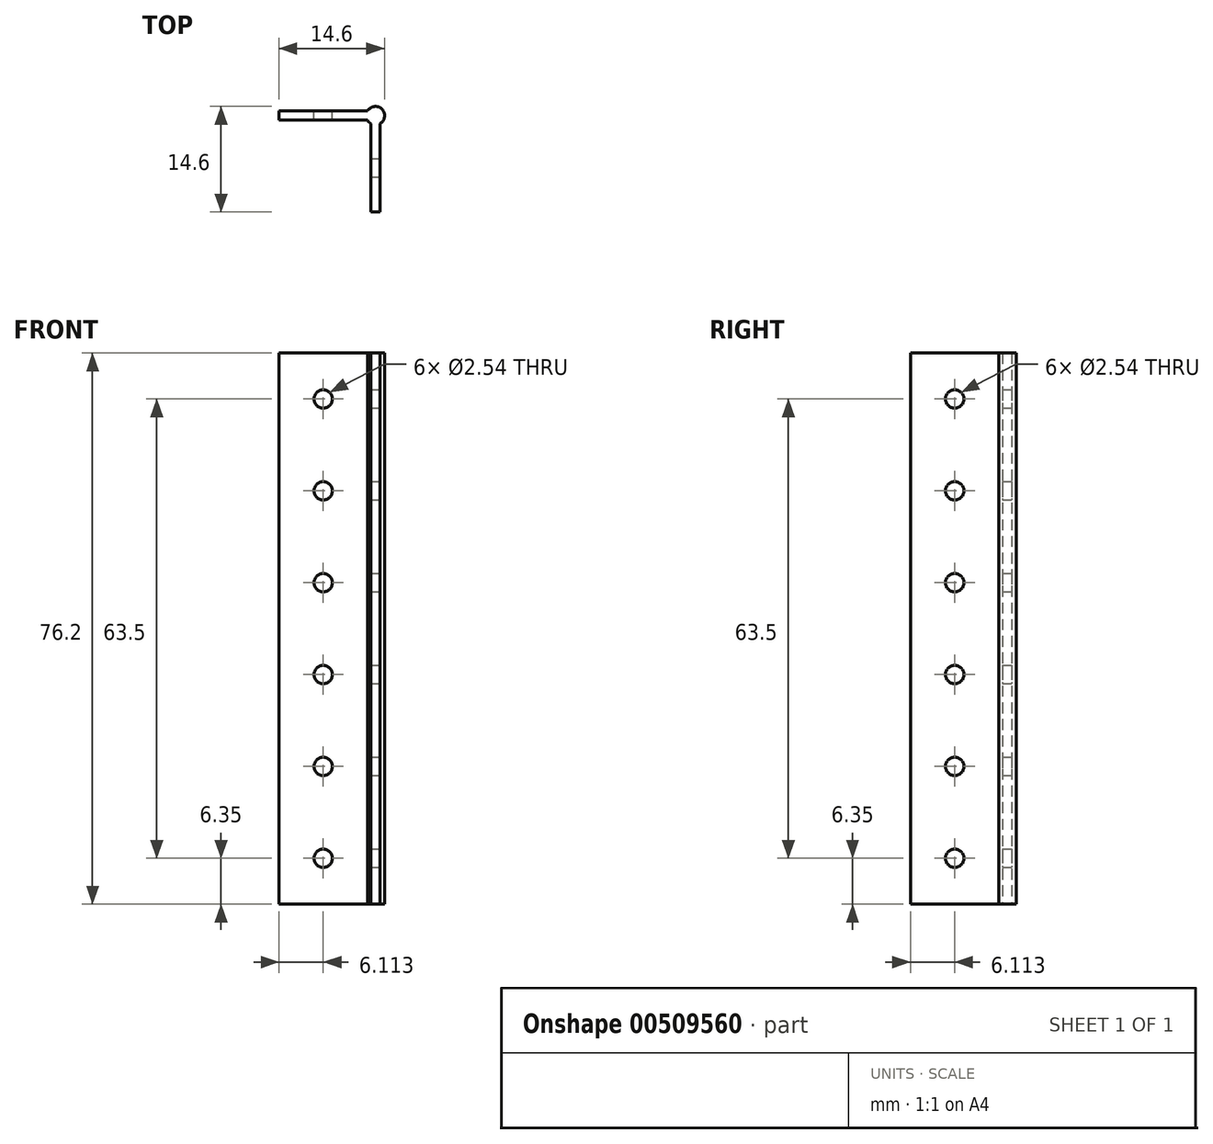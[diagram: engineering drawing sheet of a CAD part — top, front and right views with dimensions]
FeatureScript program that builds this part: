
annotation { "Feature Type Name" : "Feature", "Feature Type Description" : "" }
export const myFeature = defineFeature(function(context is Context, id is Id, definition is map)
    precondition{}
    {
        {
            var Q0;
            Q0=qCreatedBy(makeId("Top.planeOp"),FACE);
            var sketch = newSketch(context, id + "F0", { "sketchPlane" : qUnion([Q0])});
            skCircle(sketch, "E0", {"center": v(1.27, 1.27) * mm, "radius": 1.27 * mm});
            skPoint(sketch, "E0.centerSnap0", {"position": v(1.27, 0) * mm});
            skPoint(sketch, "E0.centerSnap1", {"position": v(0, 1.27) * mm});
            skLineSegment(sketch, "E1", {"start": v(1.27, 1.27) * mm, "end": v(0, 1.27) * mm});
            skLineSegment(sketch, "E2", {"start": v(1.27, 1.27) * mm, "end": v(1.27, 2.54) * mm});
            skLineSegment(sketch, "E3", {"start": v(1.27, 2.54) * mm, "end": v(0, 1.27) * mm});
            skLineSegment(sketch, "E4", {"start": v(1.27, 1.27) * mm, "end": v(1.27, 0) * mm});
            skLineSegment(sketch, "E5", {"start": v(1.27, 1.27) * mm, "end": v(2.54, 1.27) * mm});
            skLineSegment(sketch, "E6", {"start": v(2.54, 1.27) * mm, "end": v(1.27, 2.54) * mm});
            skLineSegment(sketch, "E7", {"start": v(1.27, 0) * mm, "end": v(2.54, 1.27) * mm});
            skLineSegment(sketch, "E8", {"start": v(0, 1.27) * mm, "end": v(1.27, 0) * mm});
            skLineSegment(sketch, "E9", {"start": v(0.64, 0.64) * mm, "end": v(0.64, -12.07) * mm});
            skLineSegment(sketch, "E10", {"start": v(0.64, -12.07) * mm, "end": v(1.9, -12.07) * mm});
            skPoint(sketch, "E10.endSnap0", {"position": v(1.9, 0.64) * mm});
            skLineSegment(sketch, "E11", {"start": v(1.9, -12.07) * mm, "end": v(1.9, 0.64) * mm});
            skLineSegment(sketch, "E12", {"start": v(0.64, 1.9) * mm, "end": v(-12.07, 1.9) * mm});
            skLineSegment(sketch, "E13", {"start": v(-12.07, 1.9) * mm, "end": v(-12.07, 0.64) * mm});
            skLineSegment(sketch, "E14", {"start": v(-12.07, 0.64) * mm, "end": v(0.64, 0.64) * mm});
            skSolve(sketch);
        }
        {
            var Q0;
            {var subQ0=sQuery(id+"F0.wireOp",EDGE,"E13");Q0=makeQuery(id+"F0.imprint","IMPRINT",FACE,{"disambiguationData":[TD([[makeQuery(id+"F0.imprint","IMPRINT",EDGE,{"derivedFrom":subQ0}),1.0]])]});}
            var Q1;
            {var subQ0=sQuery(id+"F0.wireOp",EDGE,"E10");Q1=makeQuery(id+"F0.imprint","IMPRINT",FACE,{"disambiguationData":[TD([[makeQuery(id+"F0.imprint","IMPRINT",EDGE,{"derivedFrom":subQ0}),1.0]])]});}
            var Q2;
            {var subQ0=sQuery(id+"F0.wireOp",EDGE,"E7");var subQ3=sQuery(id+"F0.wireOp",EDGE,"E11");var subQ5=makeQuery(id+"F0.imprint","INTERSECT",VERTEX,{"derivedFrom":[subQ0,subQ3]});Q2=makeQuery(id+"F0.imprint","IMPRINT",FACE,{"disambiguationData":[TD([[makeQuery(id+"F0.imprint","IMPRINT",EDGE,{"disambiguationData":[TD([[subQ5,1.0]])],"derivedFrom":subQ3}),-1.0]])]});}
            var Q3;
            {var subQ0=sQuery(id+"F0.wireOp",EDGE,"E6");Q3=makeQuery(id+"F0.imprint","IMPRINT",FACE,{"disambiguationData":[TD([[makeQuery(id+"F0.imprint","IMPRINT",EDGE,{"derivedFrom":subQ0}),-1.0]])]});}
            var Q4;
            Q4=makeQuery(id+"F0.imprint","IMPRINT",FACE,{"disambiguationData":[TD([[makeQuery(id+"F0.imprint","IMPRINT",EDGE,{"derivedFrom":sQuery(id+"F0.wireOp",EDGE,"E2")}),-1.0]])]});
            var Q5;
            {var subQ0=sQuery(id+"F0.wireOp",EDGE,"E4");Q5=makeQuery(id+"F0.imprint","IMPRINT",FACE,{"disambiguationData":[TD([[makeQuery(id+"F0.imprint","IMPRINT",EDGE,{"derivedFrom":subQ0}),1.0]])]});}
            var Q6;
            {var subQ0=sQuery(id+"F0.wireOp",EDGE,"E7");var subQ3=sQuery(id+"F0.wireOp",EDGE,"E11");var subQ5=makeQuery(id+"F0.imprint","INTERSECT",VERTEX,{"derivedFrom":[subQ0,subQ3]});Q6=makeQuery(id+"F0.imprint","IMPRINT",FACE,{"disambiguationData":[TD([[makeQuery(id+"F0.imprint","IMPRINT",EDGE,{"disambiguationData":[TD([[subQ5,1.0]])],"derivedFrom":subQ3}),1.0]])]});}
            var Q7;
            {var subQ1=sQuery(id+"F0.wireOp",EDGE,"E0");var subQ3=sQuery(id+"F0.wireOp",EDGE,"E9");var subQ4=makeQuery(id+"F0.imprint","INTERSECT",VERTEX,{"derivedFrom":[subQ1,subQ3]});Q7=makeQuery(id+"F0.imprint","IMPRINT",FACE,{"disambiguationData":[TD([[makeQuery(id+"F0.imprint","IMPRINT",EDGE,{"disambiguationData":[TD([[subQ4,1.0]])],"derivedFrom":subQ3}),1.0]])]});}
            var Q8;
            {var subQ0=sQuery(id+"F0.wireOp",EDGE,"E14");var subQ1=sQuery(id+"F0.wireOp",EDGE,"E0");var subQ2=makeQuery(id+"F0.imprint","INTERSECT",VERTEX,{"derivedFrom":[subQ1,subQ0]});Q8=makeQuery(id+"F0.imprint","IMPRINT",FACE,{"disambiguationData":[TD([[makeQuery(id+"F0.imprint","IMPRINT",EDGE,{"disambiguationData":[TD([[subQ2,-1.0]])],"derivedFrom":subQ1}),1.0]])]});}
            var Q9;
            {var subQ1=sQuery(id+"F0.wireOp",EDGE,"E0");var subQ3=sQuery(id+"F0.wireOp",EDGE,"E14");var subQ4=makeQuery(id+"F0.imprint","INTERSECT",VERTEX,{"derivedFrom":[subQ1,subQ3]});Q9=makeQuery(id+"F0.imprint","IMPRINT",FACE,{"disambiguationData":[TD([[makeQuery(id+"F0.imprint","IMPRINT",EDGE,{"disambiguationData":[TD([[subQ4,-1.0]])],"derivedFrom":subQ3}),1.0]])]});}
            var Q10;
            {var subQ0=sQuery(id+"F0.wireOp",EDGE,"E1");Q10=makeQuery(id+"F0.imprint","IMPRINT",FACE,{"disambiguationData":[TD([[makeQuery(id+"F0.imprint","IMPRINT",EDGE,{"derivedFrom":subQ0}),1.0]])]});}
            var Q11;
            {var subQ0=sQuery(id+"F0.wireOp",EDGE,"E1");Q11=makeQuery(id+"F0.imprint","IMPRINT",FACE,{"disambiguationData":[TD([[makeQuery(id+"F0.imprint","IMPRINT",EDGE,{"derivedFrom":subQ0}),-1.0]])]});}
            var Q12;
            {var subQ0=sQuery(id+"F0.wireOp",EDGE,"E3");var subQ3=sQuery(id+"F0.wireOp",EDGE,"E12");var subQ5=makeQuery(id+"F0.imprint","INTERSECT",VERTEX,{"derivedFrom":[subQ0,subQ3]});Q12=makeQuery(id+"F0.imprint","IMPRINT",FACE,{"disambiguationData":[TD([[makeQuery(id+"F0.imprint","IMPRINT",EDGE,{"disambiguationData":[TD([[subQ5,-1.0]])],"derivedFrom":subQ3}),1.0]])]});}
            var Q13;
            {var subQ0=sQuery(id+"F0.wireOp",EDGE,"E3");var subQ3=sQuery(id+"F0.wireOp",EDGE,"E12");var subQ5=makeQuery(id+"F0.imprint","INTERSECT",VERTEX,{"derivedFrom":[subQ0,subQ3]});Q13=makeQuery(id+"F0.imprint","IMPRINT",FACE,{"disambiguationData":[TD([[makeQuery(id+"F0.imprint","IMPRINT",EDGE,{"disambiguationData":[TD([[subQ5,-1.0]])],"derivedFrom":subQ3}),-1.0]])]});}
            extrude(context, id + "F1", {"entities" : qUnion([Q0, Q1, Q2, Q3, Q4, Q5, Q6, Q7, Q8, Q9, Q10, Q11, Q12, Q13]), "depth" : 76.2 * mm});
        }
        {
            var Q0;
            Q0=makeQuery(id+"F1.opExtrude","SWEPT_FACE",FACE,{"disambiguationData":[OSD([sQuery(id+"F0.wireOp",EDGE,"E11")])]});
            var sketch = newSketch(context, id + "F2", { "sketchPlane" : qUnion([Q0])});
            skCircle(sketch, "E15", {"center": v(-5.95, 6.35) * mm, "radius": 1.27 * mm});
            skCircle(sketch, "E16.0.1.0", {"center": v(-5.95, 19.05) * mm, "radius": 1.27 * mm});
            skCircle(sketch, "E16.0.2.0", {"center": v(-5.95, 31.75) * mm, "radius": 1.27 * mm});
            skCircle(sketch, "E16.0.3.0", {"center": v(-5.95, 44.45) * mm, "radius": 1.27 * mm});
            skCircle(sketch, "E16.0.4.0", {"center": v(-5.95, 57.15) * mm, "radius": 1.27 * mm});
            skCircle(sketch, "E16.0.5.0", {"center": v(-5.95, 69.85) * mm, "radius": 1.27 * mm});
            skLineSegment(sketch, "E16.direction1", {"start": v(-5.95, 6.35) * mm, "end": v(19.45, 6.35) * mm, "construction": true});
            skLineSegment(sketch, "E16.direction2", {"start": v(-5.95, 6.35) * mm, "end": v(-5.95, 19.05) * mm, "construction": true});
            skSolve(sketch);
        }
        {
            var Q0;
            Q0=makeQuery(id+"F2.imprint","IMPRINT",FACE,{"disambiguationData":[TD([[makeQuery(id+"F2.imprint","IMPRINT",EDGE,{"derivedFrom":sQuery(id+"F2.wireOp",EDGE,"E16.0.5.0")}),1.0]])]});
            var Q1;
            Q1=makeQuery(id+"F2.imprint","IMPRINT",FACE,{"disambiguationData":[TD([[makeQuery(id+"F2.imprint","IMPRINT",EDGE,{"derivedFrom":sQuery(id+"F2.wireOp",EDGE,"E16.0.4.0")}),1.0]])]});
            var Q2;
            Q2=makeQuery(id+"F2.imprint","IMPRINT",FACE,{"disambiguationData":[TD([[makeQuery(id+"F2.imprint","IMPRINT",EDGE,{"derivedFrom":sQuery(id+"F2.wireOp",EDGE,"E16.0.3.0")}),1.0]])]});
            var Q3;
            Q3=makeQuery(id+"F2.imprint","IMPRINT",FACE,{"disambiguationData":[TD([[makeQuery(id+"F2.imprint","IMPRINT",EDGE,{"derivedFrom":sQuery(id+"F2.wireOp",EDGE,"E16.0.2.0")}),1.0]])]});
            var Q4;
            Q4=makeQuery(id+"F2.imprint","IMPRINT",FACE,{"disambiguationData":[TD([[makeQuery(id+"F2.imprint","IMPRINT",EDGE,{"derivedFrom":sQuery(id+"F2.wireOp",EDGE,"E16.0.1.0")}),1.0]])]});
            var Q5;
            Q5=makeQuery(id+"F2.imprint","IMPRINT",FACE,{"disambiguationData":[TD([[makeQuery(id+"F2.imprint","IMPRINT",EDGE,{"derivedFrom":sQuery(id+"F2.wireOp",EDGE,"E15")}),1.0]])]});
            extrude(context, id + "F3", {"entities" : qUnion([Q0, Q1, Q2, Q3, Q4, Q5]), "operationType" : NewBodyOperationType.REMOVE, "oppositeDirection" : true, "depth" : 25.4 * mm});
        }
        {
            var Q0;
            Q0=makeQuery(id+"F1.opExtrude","SWEPT_FACE",FACE,{"disambiguationData":[OSD([sQuery(id+"F0.wireOp",EDGE,"E12")])]});
            var sketch = newSketch(context, id + "F4", { "sketchPlane" : qUnion([Q0])});
            skLineSegment(sketch, "E17", {"start": v(5.95, 0) * mm, "end": v(5.95, 6.35) * mm});
            skCircle(sketch, "E18", {"center": v(5.95, 6.35) * mm, "radius": 1.27 * mm});
            skCircle(sketch, "E19.0.1.0", {"center": v(5.95, 19.05) * mm, "radius": 1.27 * mm});
            skCircle(sketch, "E19.0.2.0", {"center": v(5.95, 31.75) * mm, "radius": 1.27 * mm});
            skCircle(sketch, "E19.0.3.0", {"center": v(5.95, 44.45) * mm, "radius": 1.27 * mm});
            skCircle(sketch, "E19.0.4.0", {"center": v(5.95, 57.15) * mm, "radius": 1.27 * mm});
            skCircle(sketch, "E19.0.5.0", {"center": v(5.95, 69.85) * mm, "radius": 1.27 * mm});
            skLineSegment(sketch, "E19.direction1", {"start": v(5.95, 6.35) * mm, "end": v(31.35, 6.35) * mm, "construction": true});
            skLineSegment(sketch, "E19.direction2", {"start": v(5.95, 6.35) * mm, "end": v(5.95, 19.05) * mm, "construction": true});
            skSolve(sketch);
        }
        {
            var Q0;
            Q0=makeQuery(id+"F4.imprint","IMPRINT",FACE,{"disambiguationData":[TD([[makeQuery(id+"F4.imprint","IMPRINT",EDGE,{"derivedFrom":sQuery(id+"F4.wireOp",EDGE,"E19.0.5.0")}),1.0]])]});
            var Q1;
            Q1=makeQuery(id+"F4.imprint","IMPRINT",FACE,{"disambiguationData":[TD([[makeQuery(id+"F4.imprint","IMPRINT",EDGE,{"derivedFrom":sQuery(id+"F4.wireOp",EDGE,"E19.0.4.0")}),1.0]])]});
            var Q2;
            Q2=makeQuery(id+"F4.imprint","IMPRINT",FACE,{"disambiguationData":[TD([[makeQuery(id+"F4.imprint","IMPRINT",EDGE,{"derivedFrom":sQuery(id+"F4.wireOp",EDGE,"E19.0.3.0")}),1.0]])]});
            var Q3;
            Q3=makeQuery(id+"F4.imprint","IMPRINT",FACE,{"disambiguationData":[TD([[makeQuery(id+"F4.imprint","IMPRINT",EDGE,{"derivedFrom":sQuery(id+"F4.wireOp",EDGE,"E19.0.2.0")}),1.0]])]});
            var Q4;
            Q4=makeQuery(id+"F4.imprint","IMPRINT",FACE,{"disambiguationData":[TD([[makeQuery(id+"F4.imprint","IMPRINT",EDGE,{"derivedFrom":sQuery(id+"F4.wireOp",EDGE,"E19.0.1.0")}),1.0]])]});
            var Q5;
            Q5=makeQuery(id+"F4.imprint","IMPRINT",FACE,{"disambiguationData":[TD([[makeQuery(id+"F4.imprint","IMPRINT",EDGE,{"derivedFrom":sQuery(id+"F4.wireOp",EDGE,"E18")}),1.0]])]});
            extrude(context, id + "F5", {"entities" : qUnion([Q0, Q1, Q2, Q3, Q4, Q5]), "operationType" : NewBodyOperationType.REMOVE, "oppositeDirection" : true, "depth" : 25.4 * mm});
        }
    });
